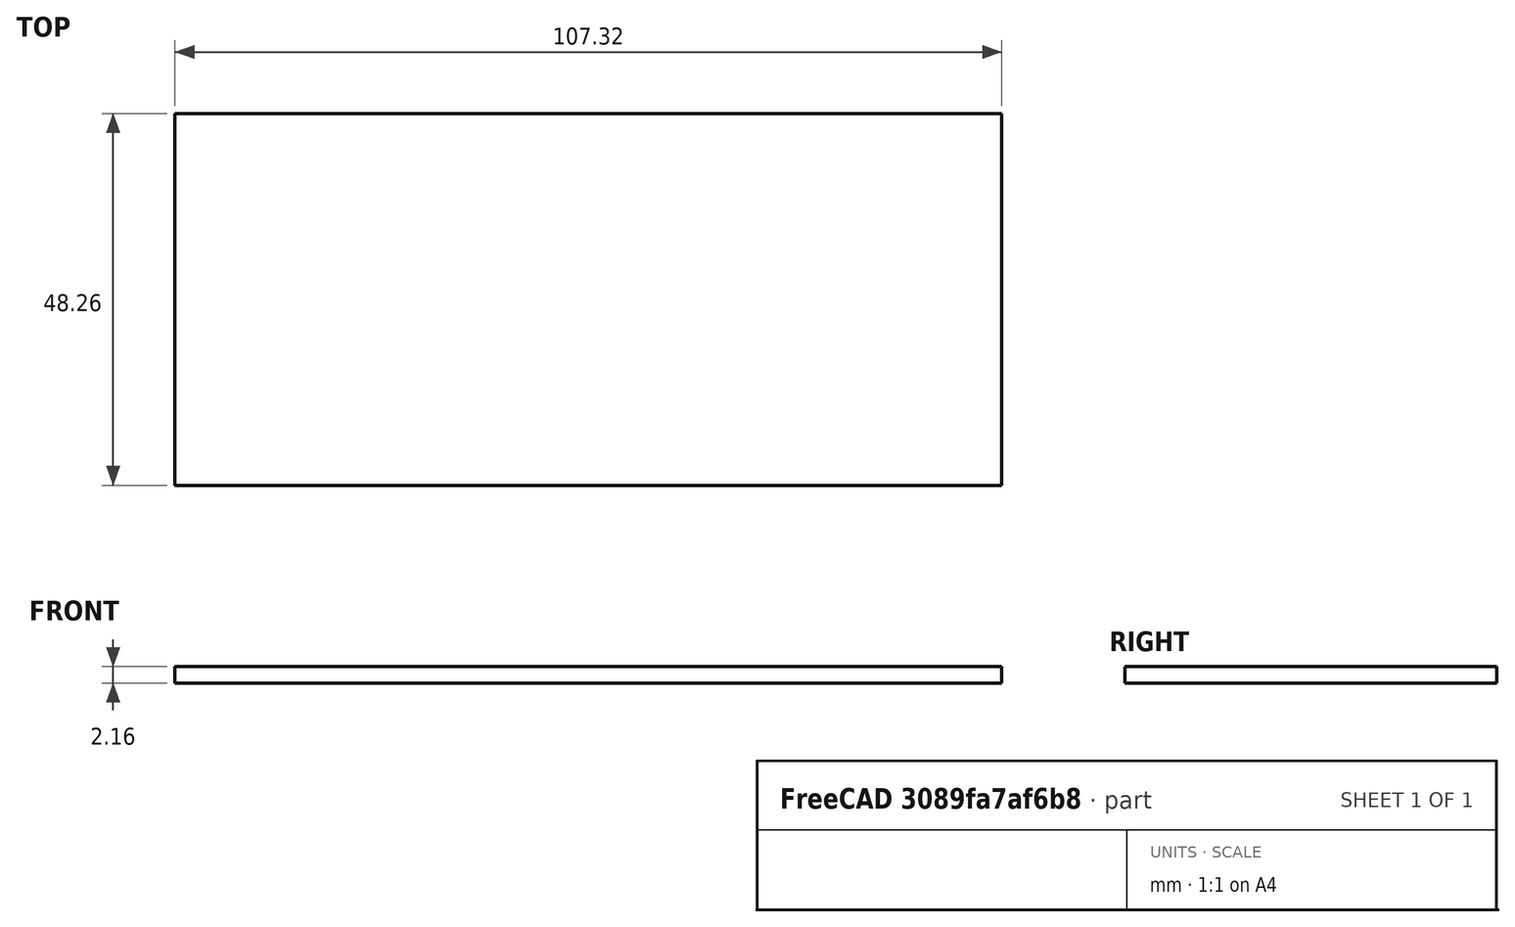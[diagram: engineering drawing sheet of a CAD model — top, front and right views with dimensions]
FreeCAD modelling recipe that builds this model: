
FCSTD DOCUMENT  (FreeCAD 0.20R29603 (Git))
Label: Big_Divider
License: All rights reserved
LicenseURL: http://en.wikipedia.org/wiki/All_rights_reserved
objects: Sketcher::SketchObject×1, PartDesign::Pad×1, PartDesign::Body×1
note: 4 computed .brp shape members not serialized (recipe doc carries the construction recipe); baked Part::Feature solids carry a one-line shape summary decoded from their .brp

FEATURE [Sketcher::SketchObject] Sketch
  FullyConstrained = true
  MapMode = 5
  Support = -> [XY_Plane]
  sketch-geometry (4):
    g0: LineSegment StartX=-53.6575 StartY=24.13 StartZ=0 EndX=53.6575 EndY=24.13 EndZ=0
    g1: LineSegment StartX=53.6575 StartY=24.13 StartZ=0 EndX=53.6575 EndY=-24.13 EndZ=0
    g2: LineSegment StartX=53.6575 StartY=-24.13 StartZ=0 EndX=-53.6575 EndY=-24.13 EndZ=0
    g3: LineSegment StartX=-53.6575 StartY=-24.13 StartZ=0 EndX=-53.6575 EndY=24.13 EndZ=0
  constraints (11):
    c: Coincident(g0,g1)
    c: Coincident(g1,g2)
    c: Coincident(g2,g3)
    c: Coincident(g3,g0)
    c: Horizontal(g0)
    c: Horizontal(g2)
    c: Vertical(g1)
    c: Vertical(g3)
    c: Symmetric(g2,g0,g-1)
    c: DistanceX(g0,g0) = 107.315
    c: DistanceY(g1,g1) = 48.26
FEATURE [PartDesign::Pad] Pad
  Direction = (0,0,1)
  Length = 2.159
  Length2 = 10
  Profile = -> Sketch
  ReferenceAxis = -> Sketch [N_Axis]
  Type = 0
FEATURE [PartDesign::Body] Body
  Group = -> [Sketch,Pad]
  Origin = -> Origin
  Tip = -> Pad
